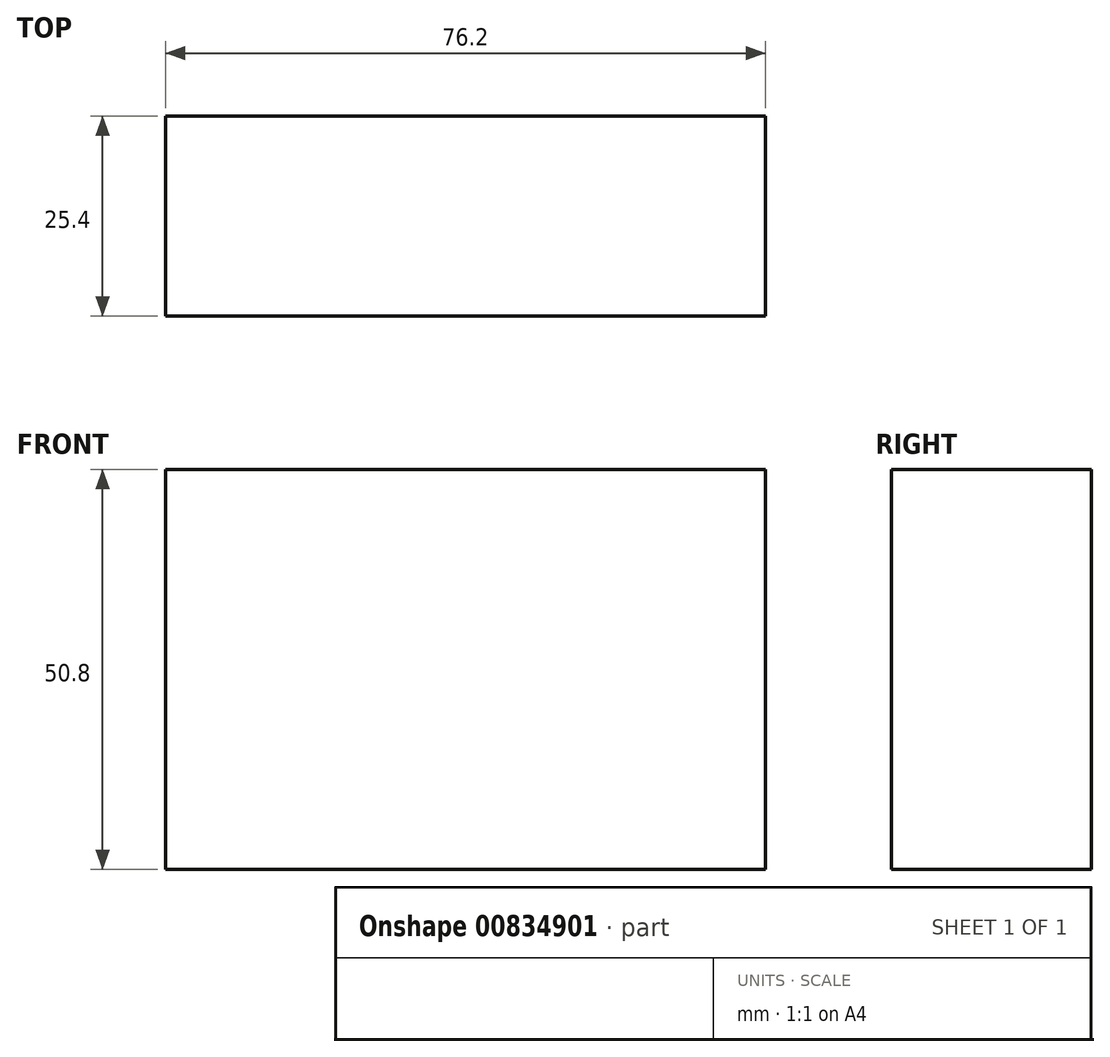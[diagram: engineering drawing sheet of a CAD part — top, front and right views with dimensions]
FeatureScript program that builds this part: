
annotation { "Feature Type Name" : "Feature", "Feature Type Description" : "" }
export const myFeature = defineFeature(function(context is Context, id is Id, definition is map)
    precondition{}
    {
        {
            var Q0;
            Q0=qCreatedBy(makeId("Front.planeOp"),FACE);
            var sketch = newSketch(context, id + "F0", { "sketchPlane" : qUnion([Q0])});
            skLineSegment(sketch, "E0.bottom", {"start": v(-63.8, 50.8) * mm, "end": v(12.4, 50.8) * mm});
            skLineSegment(sketch, "E0.top", {"start": v(-63.8, 0) * mm, "end": v(12.4, 0) * mm});
            skLineSegment(sketch, "E0.left", {"start": v(-63.8, 50.8) * mm, "end": v(-63.8, 0) * mm});
            skLineSegment(sketch, "E0.right", {"start": v(12.4, 50.8) * mm, "end": v(12.4, 0) * mm});
            skSolve(sketch);
        }
        {
            var Q0;
            Q0=makeQuery(id+"F0.imprint","IMPRINT",FACE,{"disambiguationData":[TD([[makeQuery(id+"F0.imprint","IMPRINT",EDGE,{"derivedFrom":sQuery(id+"F0.wireOp",EDGE,"E0.bottom")}),-1.0]])]});
            extrude(context, id + "F1", {"entities" : qUnion([Q0]), "depth" : 25.4 * mm, "offsetDistance" : 25.4 * mm});
        }
    });
